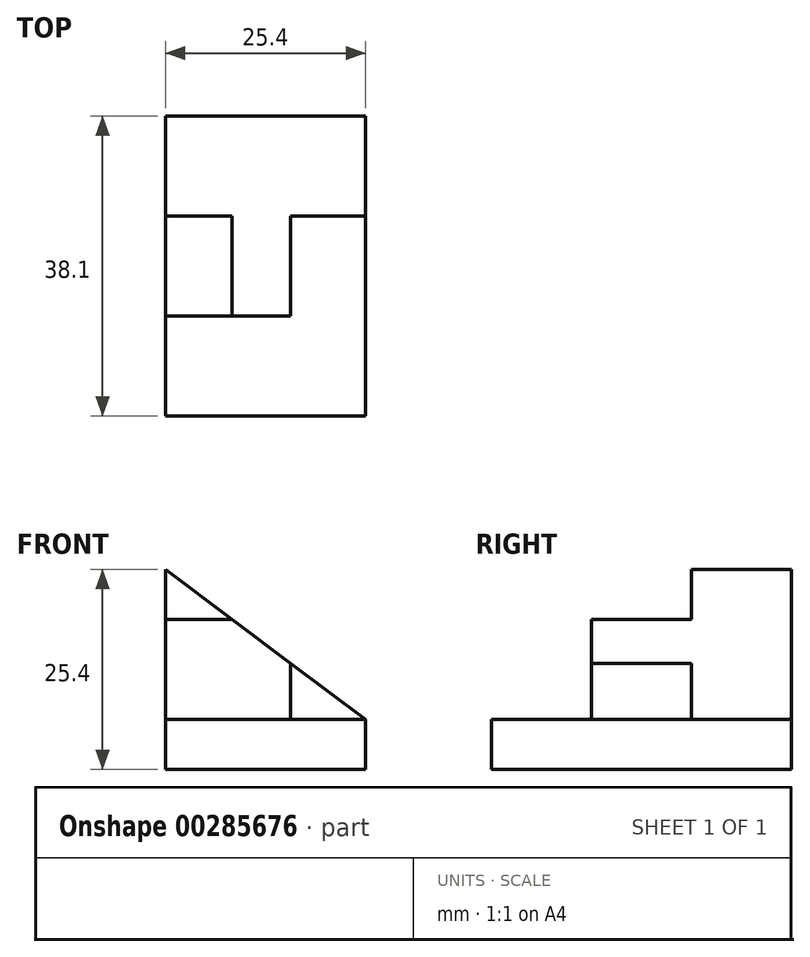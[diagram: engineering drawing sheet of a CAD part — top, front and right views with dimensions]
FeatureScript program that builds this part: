
annotation { "Feature Type Name" : "Feature", "Feature Type Description" : "" }
export const myFeature = defineFeature(function(context is Context, id is Id, definition is map)
    precondition{}
    {
        {
            var Q0;
            Q0=qCreatedBy(makeId("Front.planeOp"),FACE);
            var sketch = newSketch(context, id + "F0", { "sketchPlane" : qUnion([Q0])});
            skLineSegment(sketch, "E0", {"start": v(0, 0) * mm, "end": v(0, 6.35) * mm});
            skLineSegment(sketch, "E1", {"start": v(0, 6.35) * mm, "end": v(25.4, 6.35) * mm});
            skLineSegment(sketch, "E2", {"start": v(25.4, 6.35) * mm, "end": v(25.4, 0) * mm});
            skLineSegment(sketch, "E3", {"start": v(25.4, 0) * mm, "end": v(0, 0) * mm});
            skSolve(sketch);
        }
        {
            var Q0;
            Q0=makeQuery(id+"F0.imprint","IMPRINT",FACE,{"disambiguationData":[TD([[makeQuery(id+"F0.imprint","IMPRINT",EDGE,{"derivedFrom":sQuery(id+"F0.wireOp",EDGE,"E0")}),-1.0]])]});
            extrude(context, id + "F1", {"entities" : qUnion([Q0]), "depth" : 38.1 * mm});
        }
        {
            var Q0;
            Q0=makeQuery(id+"F1.opExtrude","CAP_FACE",FACE,{"disambiguationData":[OSD([sQuery(id+"F0.wireOp",EDGE,"E0"),sQuery(id+"F0.wireOp",EDGE,"E1"),sQuery(id+"F0.wireOp",EDGE,"E2"),sQuery(id+"F0.wireOp",EDGE,"E3")])],"isStart":true});
            var sketch = newSketch(context, id + "F2", { "sketchPlane" : qUnion([Q0])});
            skLineSegment(sketch, "E4", {"start": v(0, 6.35) * mm, "end": v(0, 25.4) * mm});
            skLineSegment(sketch, "E5", {"start": v(0, 25.4) * mm, "end": v(-25.4, 6.35) * mm});
            skLineSegment(sketch, "E6", {"start": v(-25.4, 6.35) * mm, "end": v(0, 6.35) * mm});
            skSolve(sketch);
        }
        {
            var Q0;
            Q0=makeQuery(id+"F2.imprint","IMPRINT",FACE,{"disambiguationData":[TD([[makeQuery(id+"F2.imprint","IMPRINT",EDGE,{"derivedFrom":sQuery(id+"F2.wireOp",EDGE,"E4")}),1.0]])]});
            extrude(context, id + "F3", {"entities" : qUnion([Q0]), "operationType" : NewBodyOperationType.ADD, "oppositeDirection" : true, "depth" : 12.7 * mm});
        }
        {
            var Q0;
            Q0=makeQuery(id+"F3.opExtrude","CAP_FACE",FACE,{"disambiguationData":[OSD([sQuery(id+"F2.wireOp",EDGE,"E4"),sQuery(id+"F2.wireOp",EDGE,"E5"),sQuery(id+"F2.wireOp",EDGE,"E6")])],"isStart":false});
            var sketch = newSketch(context, id + "F4", { "sketchPlane" : qUnion([Q0])});
            skLineSegment(sketch, "E7", {"start": v(0, 6.35) * mm, "end": v(0, 19.05) * mm});
            skLineSegment(sketch, "E8", {"start": v(0, 19.05) * mm, "end": v(8.47, 19.05) * mm});
            skLineSegment(sketch, "E9", {"start": v(8.47, 19.05) * mm, "end": v(15.88, 13.5) * mm});
            skLineSegment(sketch, "E10", {"start": v(15.88, 13.5) * mm, "end": v(15.88, 6.35) * mm});
            skLineSegment(sketch, "E11", {"start": v(15.88, 6.35) * mm, "end": v(0, 6.35) * mm});
            skSolve(sketch);
        }
        {
            var Q0;
            Q0=makeQuery(id+"F4.imprint","IMPRINT",FACE,{"disambiguationData":[TD([[makeQuery(id+"F4.imprint","IMPRINT",EDGE,{"derivedFrom":sQuery(id+"F4.wireOp",EDGE,"E7")}),-1.0]])]});
            extrude(context, id + "F5", {"entities" : qUnion([Q0]), "operationType" : NewBodyOperationType.ADD, "depth" : 12.7 * mm});
        }
    });
